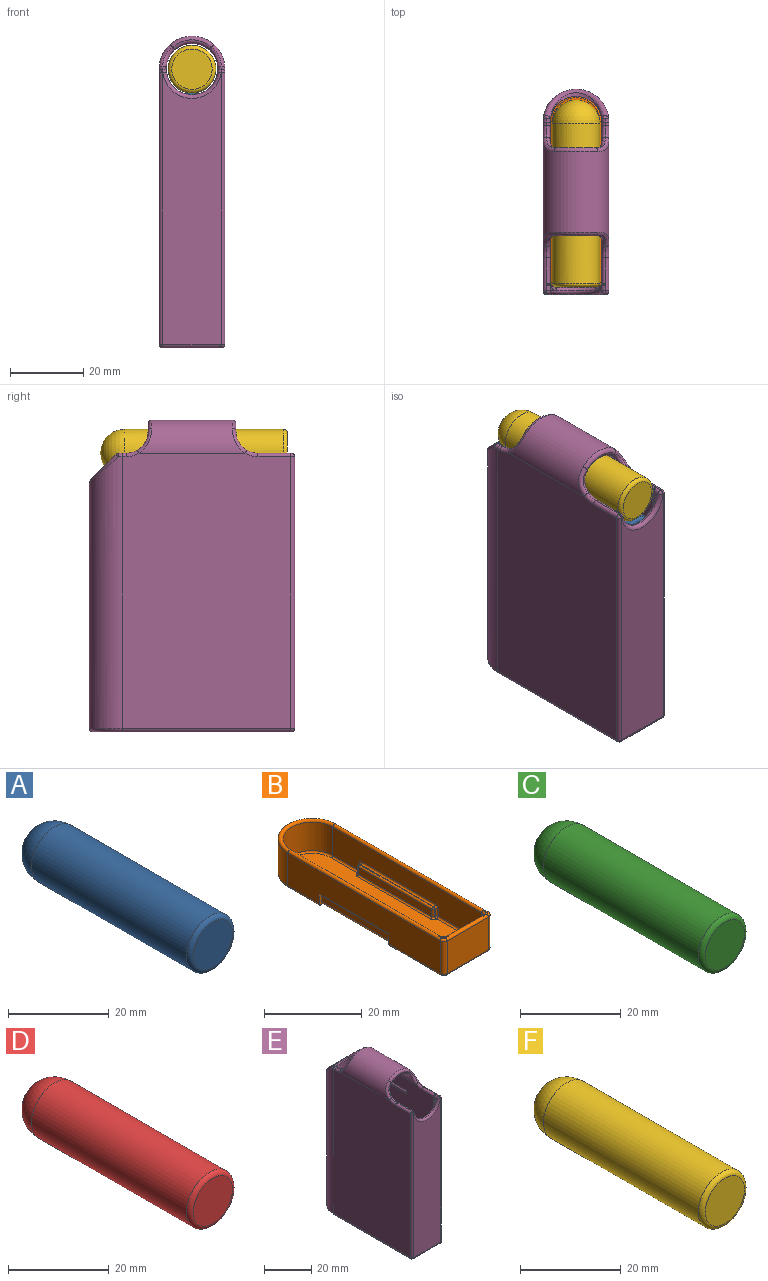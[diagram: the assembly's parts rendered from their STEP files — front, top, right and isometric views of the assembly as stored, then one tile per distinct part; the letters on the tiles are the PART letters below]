
ASSEMBLY  parts=6 mates=5
PART A: 4 faces, bbox 14.1x51x14.1 mm
  f0: cylinder r=6.5mm len=43.5mm, axis (0,1,0), area 1776.6mm2, adj f2,f3
  f1: plane 11x11mm, normal (0,-1,0), area 95mm2, adj f2
  f2: torus R=5.5mm, axis (0,-1,0), area 60.6mm2, adj f0,f1
  f3: sphere r=6.5mm, area 265.5mm2, adj f0
PART B: 96 faces, bbox 15.2x52.7x9.2 mm
  f0: plane 49.2x11.2mm, normal (0,0,1), area 492.4mm2, adj f50,f54,f55,f60,f62,f63,f65,f68
  f1: plane 43x7.1mm, normal (-1,0,0), area 246.3mm2, adj f13,f14,f24,f52,f53,f58,f61,f62
  f2: plane 44x8.2mm, normal (-1,0,0), area 310.8mm2, adj f4,f7,f8,f18,f26,f35,f37,f93
  f3: plane 44x8.2mm, normal (1,0,0), area 310.8mm2, adj f5,f7,f10,f24,f30,f32,f33,f95
  f4: cylinder r=0.5mm len=9mm, axis (0,1,0), area 7.1mm2, adj f2,f11,f28,f35
  f5: cylinder r=0.5mm len=9mm, axis (0,-1,0), area 7.1mm2, adj f3,f11,f28,f32
  f6: plane 1.5x1.5mm, normal (0,0,1), area 0.4mm2, adj f18,f19,f22,f23
  f7: cylinder r=7mm len=14mm, axis (0,0,1), area 180.3mm2, adj f2,f3,f21,f28
  f8: cylinder r=1mm len=8.2mm, axis (0,0,1), area 12.9mm2, adj f2,f9,f22,f27
  f9: plane 12x8.2mm, normal (0,-1,0), area 98.4mm2, adj f8,f10,f23,f29
  f10: cylinder r=1mm len=8.2mm, axis (0,0,1), area 12.9mm2, adj f3,f9,f25,f31
  f11: plane 51x13mm, normal (0,0,-1), area 604.8mm2, adj f4,f5,f26,f27,f28,f29,f30,f31
  f12: plane 43x7.1mm, normal (1,0,0), area 246.3mm2, adj f13,f16,f18,f68,f75,f81,f85,f88
  f13: cylinder r=6mm len=12mm, axis (0,0,-1), area 133.8mm2, adj f1,f12,f21,f65
  f14: cylinder r=1mm len=7.1mm, axis (0,0,-1), area 11.2mm2, adj f1,f15,f20,f74
  f15: plane 10x7.1mm, normal (0,1,0), area 71mm2, adj f14,f16,f23,f80
  f16: cylinder r=1mm len=7.1mm, axis (0,0,-1), area 11.2mm2, adj f12,f15,f19,f84
  f17: plane 1.5x1.5mm, normal (0,0,1), area 0.4mm2, adj f20,f23,f24,f25
  f18: cylinder r=0.5mm len=44mm, axis (0,-1,0), area 68.3mm2, adj f2,f6,f12,f19,f21,f22
  f19: torus R=1.5mm, axis (0,0,1), area 1.5mm2, adj f6,f16,f18,f23
  f20: torus R=1.5mm, axis (0,0,1), area 1.5mm2, adj f14,f17,f23,f24
  f21: torus R=6.5mm, axis (0,0,1), area 32.1mm2, adj f7,f13,f18,f24
  f22: torus R=0.5mm, axis (0,0,1), area 1mm2, adj f6,f8,f18,f23
  f23: cylinder r=0.5mm len=12mm, axis (1,0,0), area 17.3mm2, adj f6,f9,f15,f17,f19,f20,f22,f25
  f24: cylinder r=0.5mm len=44mm, axis (0,1,0), area 68.3mm2, adj f1,f3,f17,f20,f21,f25
  f25: torus R=0.5mm, axis (0,0,1), area 1mm2, adj f10,f17,f23,f24
  f26: cylinder r=0.5mm len=15mm, axis (0,1,0), area 11.8mm2, adj f2,f11,f27,f37
  f27: torus R=0.5mm, axis (0,0,1), area 1mm2, adj f8,f11,f26,f29
  f28: torus R=6.5mm, axis (0,0,1), area 16.8mm2, adj f4,f5,f7,f11
  f29: cylinder r=0.5mm len=12mm, axis (-1,0,0), area 9.4mm2, adj f9,f11,f27,f31
  f30: cylinder r=0.5mm len=15mm, axis (0,-1,0), area 11.8mm2, adj f3,f11,f31,f33
  f31: torus R=0.5mm, axis (0,0,1), area 1mm2, adj f10,f11,f29,f30
  f32: plane 3x1.5mm, normal (0,-1,0), area 2mm2, adj f3,f5,f11,f34,f94,f95
  f33: plane 3x1.5mm, normal (0,1,0), area 2mm2, adj f3,f11,f30,f34,f94,f95
  f34: plane 20x1.41mm, normal (1,0,0), area 28.1mm2, adj f32,f33,f94,f95
  f35: plane 3x1.5mm, normal (0,-1,0), area 2mm2, adj f2,f4,f11,f36,f92,f93
  f36: plane 20x1.41mm, normal (-1,0,0), area 28.1mm2, adj f35,f37,f92,f93
  f37: plane 3x1.5mm, normal (0,1,0), area 2mm2, adj f2,f11,f26,f36,f92,f93
  f38: plane 1.8x0.2mm, normal (0,-1,0), area 0.4mm2, adj f56,f57,f63,f64
  f39: plane 1.8x0.2mm, normal (0,1,0), area 0.4mm2, adj f47,f49,f53,f54
  f40: plane 21.2x1.8mm, normal (-1,0,0), area 38.2mm2, adj f47,f48,f55,f56
  f41: plane 21.2x0.2mm, normal (0,0,1), area 4.2mm2, adj f48,f49,f57,f58
  f42: plane 1.8x0.2mm, normal (0,-1,0), area 0.4mm2, adj f78,f86,f87,f91
  f43: plane 21.2x1.8mm, normal (1,0,0), area 38.2mm2, adj f67,f77,f78,f79
  f44: plane 1.8x0.2mm, normal (0,1,0), area 0.4mm2, adj f67,f69,f75,f76
  f45: plane 21.2x0.2mm, normal (0,0,1), area 4.2mm2, adj f76,f77,f85,f86
  f46: sphere r=0.4mm, area 0.3mm2, adj f47,f48,f49
  f47: cylinder r=0.4mm len=1.8mm, axis (0,0,1), area 1.1mm2, adj f39,f40,f46,f50
  f48: cylinder r=0.4mm len=21.2mm, axis (0,1,0), area 13.3mm2, adj f40,f41,f46,f51
  f49: cylinder r=0.4mm len=0.4mm, axis (1,0,0), area 0.1mm2, adj f39,f41,f46,f52
  f50: torus R=0.8mm, axis (0,0,1), area 0.5mm2, adj f0,f47,f54,f55
  f51: sphere r=0.4mm, area 0.3mm2, adj f48,f56,f57
  f52: torus R=0.8mm, axis (1,0,0), area 0.5mm2, adj f1,f49,f53,f58
  f53: cylinder r=0.4mm len=1.8mm, axis (0,0,1), area 1.1mm2, adj f1,f39,f52,f59
  f54: cylinder r=0.4mm len=0.4mm, axis (-1,0,0), area 0.1mm2, adj f0,f39,f50,f59
  f55: cylinder r=0.4mm len=21.2mm, axis (0,-1,0), area 13.3mm2, adj f0,f40,f50,f60
  f56: cylinder r=0.4mm len=1.8mm, axis (0,0,-1), area 1.1mm2, adj f38,f40,f51,f60
  f57: cylinder r=0.4mm len=0.4mm, axis (-1,0,0), area 0.1mm2, adj f38,f41,f51,f61
  f58: cylinder r=0.4mm len=21.2mm, axis (0,-1,0), area 13.3mm2, adj f1,f41,f52,f61
  f59: sphere r=0.4mm, area 0.3mm2, adj f53,f54,f62
  f60: torus R=0.8mm, axis (0,0,1), area 0.5mm2, adj f0,f55,f56,f63
  f61: torus R=0.8mm, axis (1,0,0), area 0.5mm2, adj f1,f57,f58,f64
  f62: cylinder r=0.4mm len=7.6mm, axis (0,-1,0), area 4.8mm2, adj f0,f1,f59,f65
  f63: cylinder r=0.4mm len=0.4mm, axis (1,0,0), area 0.1mm2, adj f0,f38,f60,f66
  f64: cylinder r=0.4mm len=1.8mm, axis (0,0,-1), area 1.1mm2, adj f1,f38,f61,f66
  f65: torus R=5.6mm, axis (0,0,1), area 11.6mm2, adj f0,f13,f62,f68
  f66: sphere r=0.4mm, area 0.3mm2, adj f63,f64,f70
  f67: cylinder r=0.4mm len=1.8mm, axis (0,0,1), area 1.1mm2, adj f43,f44,f72,f73
  f68: cylinder r=0.4mm len=7.6mm, axis (0,1,0), area 4.8mm2, adj f0,f12,f65,f71
  f69: cylinder r=0.4mm len=0.4mm, axis (-1,0,0), area 0.1mm2, adj f0,f44,f71,f73
  f70: cylinder r=0.4mm len=12.6mm, axis (0,-1,0), area 7.9mm2, adj f0,f1,f66,f74
  f71: sphere r=0.4mm, area 0.3mm2, adj f68,f69,f75
  f72: sphere r=0.4mm, area 0.3mm2, adj f67,f76,f77
  f73: torus R=0.8mm, axis (0,0,1), area 0.5mm2, adj f0,f67,f69,f79
  f74: torus R=0.6mm, axis (0,0,1), area 0.8mm2, adj f0,f14,f70,f80
  f75: cylinder r=0.4mm len=1.8mm, axis (0,0,1), area 1.1mm2, adj f12,f44,f71,f81
  f76: cylinder r=0.4mm len=0.4mm, axis (1,0,0), area 0.1mm2, adj f44,f45,f72,f81
  f77: cylinder r=0.4mm len=21.2mm, axis (0,-1,0), area 13.3mm2, adj f43,f45,f72,f82
  f78: cylinder r=0.4mm len=1.8mm, axis (0,0,-1), area 1.1mm2, adj f42,f43,f82,f83
  f79: cylinder r=0.4mm len=21.2mm, axis (0,1,0), area 13.3mm2, adj f0,f43,f73,f83
  f80: cylinder r=0.4mm len=10mm, axis (-1,0,0), area 6.3mm2, adj f0,f15,f74,f84
  f81: torus R=0.8mm, axis (1,0,0), area 0.5mm2, adj f12,f75,f76,f85
  f82: sphere r=0.4mm, area 0.3mm2, adj f77,f78,f86
  f83: torus R=0.8mm, axis (0,0,1), area 0.5mm2, adj f0,f78,f79,f87
  f84: torus R=0.6mm, axis (0,0,1), area 0.8mm2, adj f0,f16,f80,f88
  f85: cylinder r=0.4mm len=21.2mm, axis (0,1,0), area 13.3mm2, adj f12,f45,f81,f89
  f86: cylinder r=0.4mm len=0.4mm, axis (-1,0,0), area 0.1mm2, adj f42,f45,f82,f89
  f87: cylinder r=0.4mm len=0.4mm, axis (1,0,0), area 0.1mm2, adj f0,f42,f83,f90
  f88: cylinder r=0.4mm len=12.6mm, axis (0,1,0), area 7.9mm2, adj f0,f12,f84,f90
  f89: torus R=0.8mm, axis (1,0,0), area 0.5mm2, adj f12,f85,f86,f91
  f90: sphere r=0.4mm, area 0.3mm2, adj f87,f88,f91
  f91: cylinder r=0.4mm len=1.8mm, axis (0,0,-1), area 1.1mm2, adj f12,f42,f89,f90
  f92: cylinder r=0.8mm len=20mm, axis (0,-1,0), area 25.1mm2, adj f11,f35,f36,f37
  f93: cylinder r=0.8mm len=20mm, axis (0,1,0), area 23.1mm2, adj f2,f35,f36,f37
  f94: cylinder r=0.8mm len=20mm, axis (0,1,0), area 25.1mm2, adj f11,f32,f33,f34
  f95: cylinder r=0.8mm len=20mm, axis (0,1,0), area 23.1mm2, adj f3,f32,f33,f34
PART C: 4 faces, bbox 14.1x51x14.1 mm
  f0: cylinder r=6.5mm len=43.5mm, axis (0,1,0), area 1776.6mm2, adj f2,f3
  f1: plane 11x11mm, normal (0,-1,0), area 95mm2, adj f2
  f2: torus R=5.5mm, axis (0,-1,0), area 60.6mm2, adj f0,f1
  f3: sphere r=6.5mm, area 265.5mm2, adj f0
PART D: 4 faces, bbox 14.1x51x14.1 mm
  f0: cylinder r=6.5mm len=43.5mm, axis (0,1,0), area 1776.6mm2, adj f2,f3
  f1: plane 11x11mm, normal (0,-1,0), area 95mm2, adj f2
  f2: torus R=5.5mm, axis (0,-1,0), area 60.6mm2, adj f0,f1
  f3: sphere r=6.5mm, area 265.5mm2, adj f0
PART E: 94 faces, bbox 19.5x56.7x85.7 mm
  f0: plane 72x44mm, normal (1,0,0), area 3125.6mm2, adj f11,f15,f19,f33,f35,f59,f63,f83
  f1: cylinder r=7mm len=3.76mm, axis (0,-1,0), area 3.1mm2, adj f22,f24,f27
  f2: plane 2x0.06mm, normal (0,0,1), area 0.1mm2, adj f27,f28,f31,f32
  f3: plane 74x16mm, normal (0,-1,0), area 1099.4mm2, adj f7,f8,f22,f28,f41,f77
  f4: plane 2x0.06mm, normal (0,0,1), area 0.1mm2, adj f41,f47,f48,f51
  f5: cylinder r=9mm len=74mm, axis (0,0,1), area 1975.5mm2, adj f6,f9,f25,f53,f61,f76
  f6: plane 75x46mm, normal (-1,0,0), area 3435.1mm2, adj f5,f7,f20,f32,f34,f55,f58,f74
  f7: cylinder r=1mm len=74mm, axis (0,0,1), area 116.2mm2, adj f3,f6,f30,f75
  f8: cylinder r=1mm len=74mm, axis (0,0,1), area 116.2mm2, adj f3,f9,f44,f79
  f9: plane 75x46mm, normal (1,0,0), area 3435.1mm2, adj f5,f8,f20,f43,f47,f65,f69,f78
  f10: plane 54x16mm, normal (0,0,-1), area 836.5mm2, adj f74,f76,f77,f78
  f11: cylinder r=7mm len=71mm, axis (0,0,-1), area 1484.4mm2, adj f0,f12,f18,f56,f64,f89
  f12: plane 72x44mm, normal (-1,0,0), area 3125.6mm2, adj f11,f13,f19,f46,f49,f68,f72,f80
  f13: cylinder r=1mm len=71mm, axis (0,0,-1), area 108.7mm2, adj f12,f14,f21,f51,f90
  f14: plane 66.71x12mm, normal (0,1,0), area 778mm2, adj f13,f15,f23,f92
  f15: cylinder r=1mm len=71mm, axis (0,0,-1), area 108.7mm2, adj f0,f14,f24,f31,f93
  f16: plane 48x10mm, normal (0,0,1), area 469.3mm2, adj f88,f89,f91,f92
  f17: cylinder r=7mm len=3.76mm, axis (0,-1,0), area 3.1mm2, adj f21,f22,f48
  f18: cylinder r=7mm len=13.89mm, axis (0,-1,0), area 13.9mm2, adj f11,f25,f54,f56,f60,f64
  f19: cylinder r=7mm len=28.79mm, axis (0,1,0), area 524.1mm2, adj f0,f12,f37,f39,f42,f67,f71,f73
  f20: cylinder r=9mm len=28.79mm, axis (0,1,0), area 673.9mm2, adj f6,f9,f36,f38,f40,f62,f66,f70
  f21: bspline ~5.19x2.15mm, area 4mm2, adj f13,f17,f23,f50
  f22: torus R=8mm, axis (0,1,0), area 33.4mm2, adj f1,f3,f17,f23,f26,f45
  f23: torus R=8mm, axis (0,-1,0), area 19.6mm2, adj f14,f21,f22,f24
  f24: bspline ~5.19x2.15mm, area 4mm2, adj f1,f15,f23,f29
  f25: bspline ~17.85x8mm, area 59.7mm2, adj f5,f18,f52,f57
  f26: sphere r=1mm, area 2mm2, adj f22,f27,f28
  f27: cylinder r=1mm len=1.5mm, axis (0,-1,0), area 2.2mm2, adj f1,f2,f26,f29
  f28: cylinder r=1mm len=1mm, axis (-1,0,0), area 0.1mm2, adj f2,f3,f26,f30
  f29: sphere r=1mm, area 0.1mm2, adj f24,f27,f31
  f30: sphere r=1mm, area 1.6mm2, adj f7,f28,f32
  f31: torus R=2mm, axis (0,0,1), area 0.5mm2, adj f2,f15,f29,f33
  f32: cylinder r=1mm len=9mm, axis (0,-1,0), area 14.1mm2, adj f2,f6,f30,f33,f34
  f33: cylinder r=1mm len=7mm, axis (0,-1,0), area 11mm2, adj f0,f31,f32,f35
  f34: torus R=7mm, axis (-1,0,0), area 5.4mm2, adj f6,f32,f35,f36
  f35: torus R=7mm, axis (1,0,0), area 5.4mm2, adj f0,f33,f34,f37
  f36: bspline ~7.65x4.43mm, area 11.5mm2, adj f20,f34,f37,f38
  f37: bspline ~7.09x4.63mm, area 11.5mm2, adj f19,f35,f36,f39
  f38: torus R=8mm, axis (0,-1,0), area 19.6mm2, adj f20,f36,f39,f40
  f39: torus R=8mm, axis (0,-1,0), area 16.7mm2, adj f19,f37,f38,f42
  f40: bspline ~7.65x4.43mm, area 11.5mm2, adj f20,f38,f42,f43
  f41: cylinder r=1mm len=1mm, axis (-1,0,0), area 0.1mm2, adj f3,f4,f44,f45
  f42: bspline ~7.09x4.63mm, area 11.5mm2, adj f19,f39,f40,f46
  f43: torus R=7mm, axis (-1,0,0), area 5.4mm2, adj f9,f40,f46,f47
  f44: sphere r=1mm, area 1.6mm2, adj f8,f41,f47
  f45: sphere r=1mm, area 0.9mm2, adj f22,f41,f48
  f46: torus R=7mm, axis (1,0,0), area 5.4mm2, adj f12,f42,f43,f49
  f47: cylinder r=1mm len=9mm, axis (0,1,0), area 14.1mm2, adj f4,f9,f43,f44,f49
  f48: cylinder r=1mm len=1.5mm, axis (0,-1,0), area 2.2mm2, adj f4,f17,f45,f50
  f49: cylinder r=1mm len=7mm, axis (0,1,0), area 11mm2, adj f12,f46,f47,f51
  f50: sphere r=1mm, area 0.2mm2, adj f21,f48,f51
  f51: torus R=2mm, axis (0,0,1), area 0.5mm2, adj f4,f13,f49,f50
  f52: bspline ~1.99x1.02mm, area 1.5mm2, adj f25,f53,f54
  f53: torus R=8mm, axis (0,0,1), area 1.7mm2, adj f5,f52,f55,f56
  f54: cylinder r=1mm len=0.99mm, axis (0,-1,0), area 0mm2, adj f18,f52,f56
  f55: cylinder r=1mm len=1mm, axis (0,-1,0), area 1.6mm2, adj f6,f53,f58,f59
  f56: torus R=8mm, axis (0,0,1), area 1.5mm2, adj f11,f18,f53,f54,f59
  f57: bspline ~1.99x1.02mm, area 1.5mm2, adj f25,f60,f61
  f58: torus R=7mm, axis (-1,0,0), area 5.4mm2, adj f6,f55,f62,f63
  f59: cylinder r=1mm len=1mm, axis (0,-1,0), area 1.6mm2, adj f0,f55,f56,f63
  f60: cylinder r=1mm len=0.99mm, axis (0,-1,0), area 0mm2, adj f18,f57,f64
  f61: torus R=8mm, axis (0,0,1), area 1.7mm2, adj f5,f57,f64,f65
  f62: bspline ~7.65x4.43mm, area 11.5mm2, adj f20,f58,f66,f67
  f63: torus R=7mm, axis (1,0,0), area 5.4mm2, adj f0,f58,f59,f67
  f64: torus R=8mm, axis (0,0,1), area 1.5mm2, adj f11,f18,f60,f61,f68
  f65: cylinder r=1mm len=1mm, axis (0,1,0), area 1.6mm2, adj f9,f61,f68,f69
  f66: torus R=8mm, axis (0,-1,0), area 19.6mm2, adj f20,f62,f70,f71
  f67: bspline ~7.09x4.63mm, area 11.5mm2, adj f19,f62,f63,f71
  f68: cylinder r=1mm len=1mm, axis (0,1,0), area 1.6mm2, adj f12,f64,f65,f72
  f69: torus R=7mm, axis (-1,0,0), area 5.4mm2, adj f9,f65,f70,f72
  f70: bspline ~7.65x4.43mm, area 11.5mm2, adj f20,f66,f69,f73
  f71: torus R=8mm, axis (0,-1,0), area 16.7mm2, adj f19,f66,f67,f73
  f72: torus R=7mm, axis (1,0,0), area 5.4mm2, adj f12,f68,f69,f73
  f73: bspline ~7.09x4.63mm, area 11.5mm2, adj f19,f70,f71,f72
  f74: cylinder r=1mm len=46mm, axis (0,1,0), area 72.3mm2, adj f6,f10,f75,f76
  f75: sphere r=1mm, area 1.6mm2, adj f7,f74,f77
  f76: torus R=8mm, axis (0,0,1), area 42.6mm2, adj f5,f10,f74,f78
  f77: cylinder r=1mm len=16mm, axis (-1,0,0), area 25.1mm2, adj f3,f10,f75,f79
  f78: cylinder r=1mm len=46mm, axis (0,-1,0), area 72.3mm2, adj f9,f10,f76,f79
  f79: sphere r=1mm, area 2.1mm2, adj f8,f77,f78
  f80: cylinder r=0.6mm len=1.64mm, axis (0,0,-1), area 0.7mm2, adj f12,f81,f86
  f81: cylinder r=0.6mm len=18mm, axis (0,1,0), area 27.3mm2, adj f12,f80,f82,f86
  f82: cylinder r=0.6mm len=1.64mm, axis (0,0,1), area 0.7mm2, adj f12,f81,f86
  f83: cylinder r=0.6mm len=1.64mm, axis (0,0,1), area 0.7mm2, adj f0,f84,f87
  f84: cylinder r=0.6mm len=18mm, axis (0,-1,0), area 27.3mm2, adj f0,f83,f85,f87
  f85: cylinder r=0.6mm len=1.64mm, axis (0,0,-1), area 0.7mm2, adj f0,f84,f87
  f86: cylinder r=0.6mm len=18mm, axis (0,1,0), area 11.3mm2, adj f12,f80,f81,f82
  f87: cylinder r=0.6mm len=18mm, axis (0,-1,0), area 11.3mm2, adj f0,f83,f84,f85
  f88: cylinder r=2mm len=44mm, axis (0,-1,0), area 136.7mm2, adj f12,f16,f89,f90
  f89: torus R=5mm, axis (0,0,1), area 61.9mm2, adj f11,f16,f88,f91
  f90: bspline ~2.39x2mm, area 2.2mm2, adj f13,f88,f92
  f91: cylinder r=2mm len=44mm, axis (0,1,0), area 136.7mm2, adj f0,f16,f89,f93
  f92: cylinder r=2mm len=12mm, axis (-1,0,0), area 34.6mm2, adj f14,f16,f90,f93
  f93: bspline ~2.39x2mm, area 2.2mm2, adj f15,f91,f92
PART F: 4 faces, bbox 14.1x51x14.1 mm
  f0: cylinder r=6.5mm len=43.5mm, axis (0,1,0), area 1776.6mm2, adj f2,f3
  f1: plane 11x11mm, normal (0,-1,0), area 95mm2, adj f2
  f2: torus R=5.5mm, axis (0,-1,0), area 60.6mm2, adj f0,f1
  f3: sphere r=6.5mm, area 265.5mm2, adj f0
PLACE A rot(axis=(0,1,0),90deg) t=(1.8,-14.88,93.44)mm
PLACE B rot(axis=(0,1,0),180deg) t=(1.8,-14.18,33.74)mm
PLACE C rot(axis=(0,1,0),90deg) t=(1.8,-14.88,67.44)mm
PLACE D rot(axis=(0,1,0),90deg) t=(1.8,-14.88,41.44)mm
PLACE E t=(1.8,-14.38,6.44)mm
PLACE F rot(axis=(0,1,0),90deg) t=(1.8,-14.88,119.44)mm
MATE slider C.f0 <-> E.f14  axis (0,-1,0) through (1.8,-40.38,54.44)mm
MATE slider F.f0 <-> E.f1  axis (0,-1,0) through (1.8,-40.38,80.44)mm
MATE slider A.f0 <-> E.f14  axis (0,-1,0) through (1.8,-40.38,67.44)mm
MATE slider D.f0 <-> E.f14  axis (0,-1,0) through (1.8,-40.38,41.44)mm
MATE slider B.f11 <-> E.f16  axis (0,0,1) through (1.8,-14.9,34.94)mm
